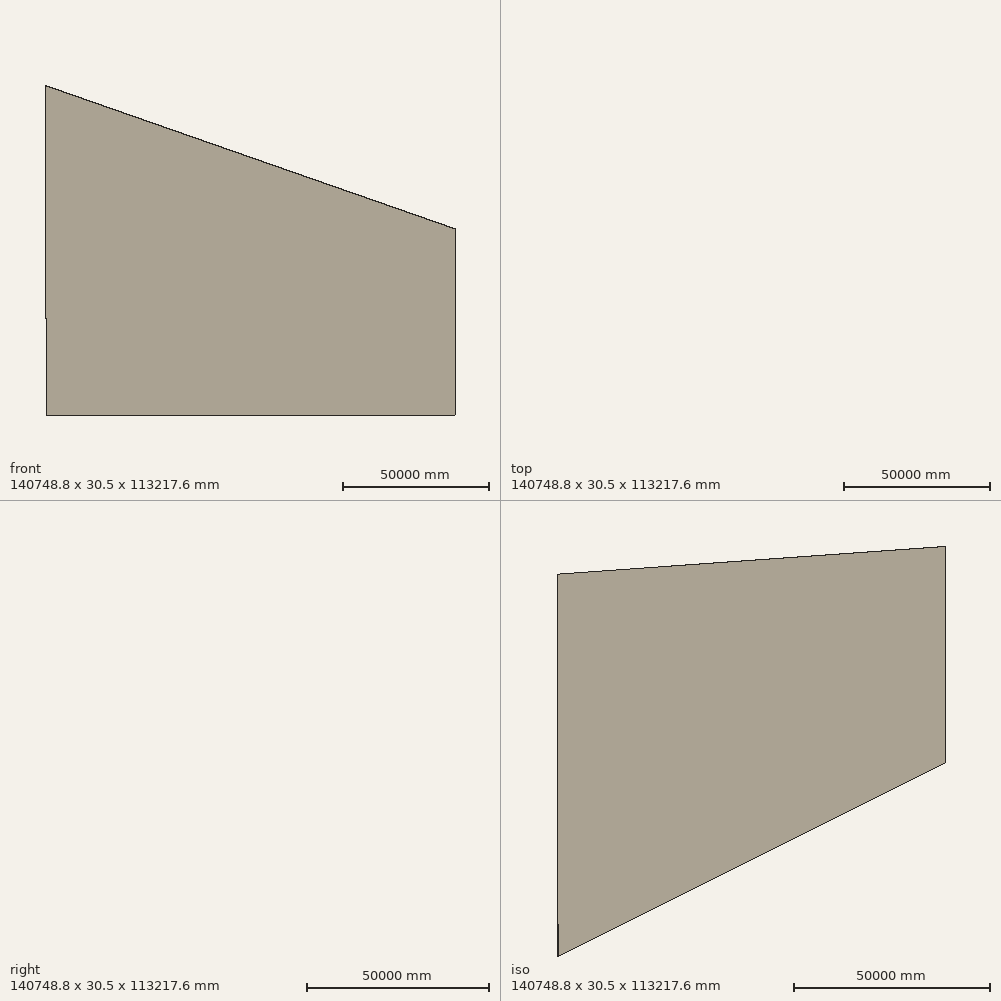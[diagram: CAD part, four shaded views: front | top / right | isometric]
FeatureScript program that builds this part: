
annotation { "Feature Type Name" : "Feature", "Feature Type Description" : "" }
export const myFeature = defineFeature(function(context is Context, id is Id, definition is map)
    precondition{}
    {
        {
            var Q0;
            Q0=qCreatedBy(makeId("Front.planeOp"),FACE);
            var sketch = newSketch(context, id + "F0", { "sketchPlane" : qUnion([Q0])});
            skLineSegment(sketch, "E0", {"start": v(0, 0) * mm, "end": v(140485.37, 0) * mm});
            skLineSegment(sketch, "E1", {"start": v(0, 0) * mm, "end": v(-263.46, 113217.65) * mm});
            skLineSegment(sketch, "E2", {"start": v(0, 0) * mm, "end": v(0, 157788.57) * mm, "construction": true});
            skLineSegment(sketch, "E3", {"start": v(-263.46, 113217.65) * mm, "end": v(140350.35, 64021.4) * mm});
            skLineSegment(sketch, "E4", {"start": v(140485.37, 0) * mm, "end": v(140485.37, 84521.6) * mm, "construction": true});
            skLineSegment(sketch, "E5", {"start": v(140485.37, 0) * mm, "end": v(140350.35, 64021.4) * mm});
            skSolve(sketch);
        }
        {
            var Q0;
            Q0=makeQuery(id+"F0.imprint","IMPRINT",FACE,{"disambiguationData":[TD([[makeQuery(id+"F0.imprint","IMPRINT",EDGE,{"derivedFrom":sQuery(id+"F0.wireOp",EDGE,"E0")}),1.0]])]});
            extrude(context, id + "F1", {"entities" : qUnion([Q0]), "depth" : 30.48 * mm, "offsetDistance" : 30.48 * mm});
        }
    });
